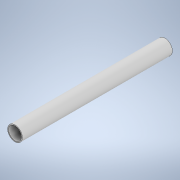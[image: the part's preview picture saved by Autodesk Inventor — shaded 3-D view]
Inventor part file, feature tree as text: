
AUTODESK INVENTOR PART (.ipt)
format: ipt  version: 2022.2 (Build 262287000, 287)  size: 97,792 bytes
history: native  units: in
note: dims shown in document units (in); Inventor stores cm internally (conversion verified against a paired STEP export)
features: extrude x1, sketch x1
ambient origin geometry x8: Origin, YZ Plane, XZ Plane, XY Plane, X Axis, Y Axis, Z Axis, Center Point
bodies: Solid1 (feature_tree)
feature tree (2):
  extrude  "Extrusion1"  Depth=24.0in
  sketch  "Sketch1"  dims[d0=2.375in d1=2.067in d2=24.0in d3=0.0in]
